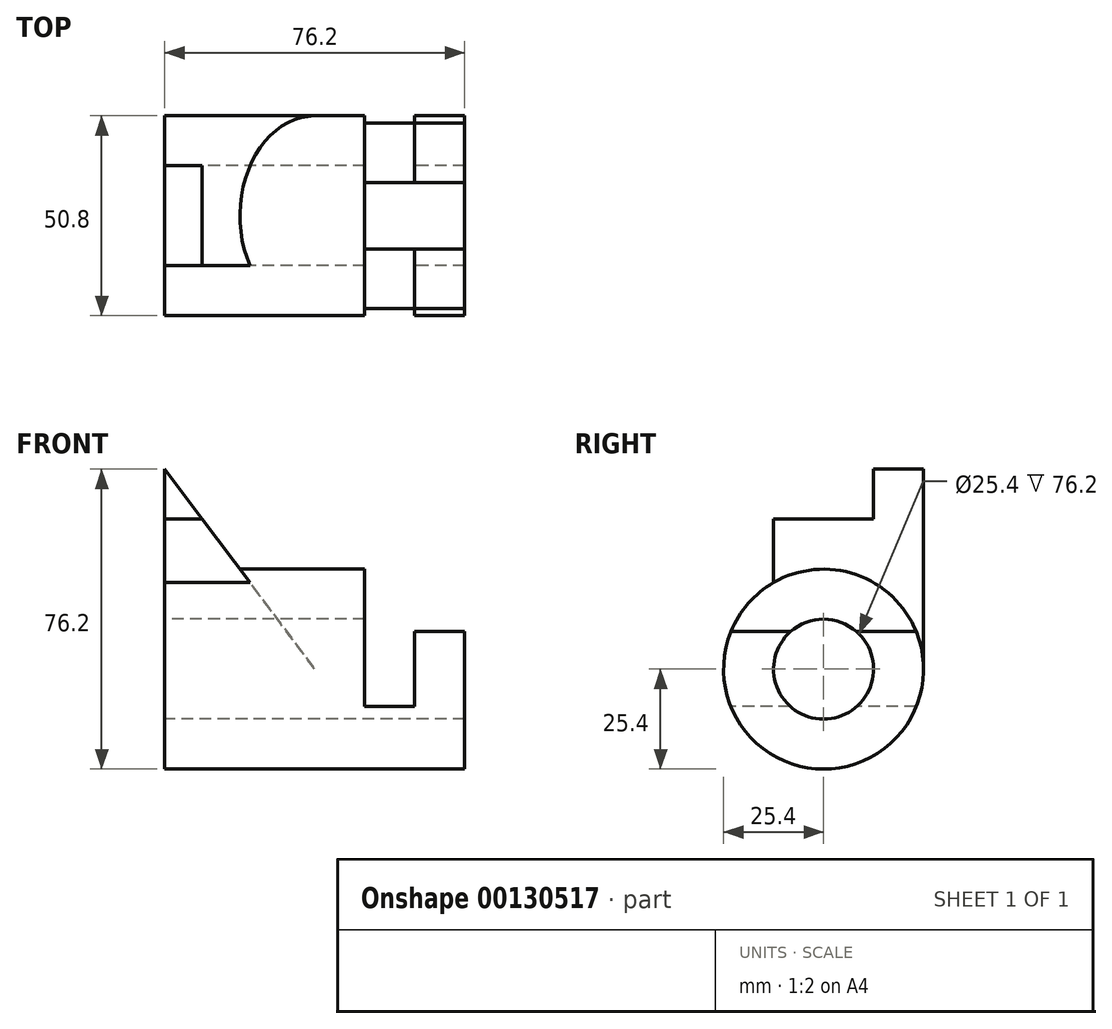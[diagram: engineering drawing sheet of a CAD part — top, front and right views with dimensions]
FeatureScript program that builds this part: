
annotation { "Feature Type Name" : "Feature", "Feature Type Description" : "" }
export const myFeature = defineFeature(function(context is Context, id is Id, definition is map)
    precondition{}
    {
        {
            var Q0;
            Q0=qCreatedBy(makeId("Right.planeOp"),FACE);
            var sketch = newSketch(context, id + "F0", { "sketchPlane" : qUnion([Q0])});
            skCircle(sketch, "E0", {"center": v(0, 0) * mm, "radius": 25.4 * mm});
            skCircle(sketch, "E1", {"center": v(0, 0) * mm, "radius": 12.7 * mm});
            skSolve(sketch);
        }
        {
            var Q0;
            Q0=makeQuery(id+"F0.imprint","IMPRINT",FACE,{"disambiguationData":[TD([[makeQuery(id+"F0.imprint","IMPRINT",EDGE,{"derivedFrom":sQuery(id+"F0.wireOp",EDGE,"E0")}),1.0]])]});
            extrude(context, id + "F1", {"entities" : qUnion([Q0]), "endBound" : BoundingType.SYMMETRIC, "depth" : 76.2 * mm});
        }
        {
            var Q0;
            Q0=qCreatedBy(makeId("Front.planeOp"),FACE);
            var sketch = newSketch(context, id + "F2", { "sketchPlane" : qUnion([Q0])});
            skLineSegment(sketch, "E2.bottom", {"start": v(0, 0) * mm, "end": v(-38.1, 0) * mm});
            skLineSegment(sketch, "E2.top", {"start": v(0, 50.8) * mm, "end": v(-38.1, 50.8) * mm});
            skLineSegment(sketch, "E2.left", {"start": v(0, 0) * mm, "end": v(0, 50.8) * mm});
            skLineSegment(sketch, "E2.right", {"start": v(-38.1, 0) * mm, "end": v(-38.1, 50.8) * mm});
            skLineSegment(sketch, "E3", {"start": v(-38.1, 50.8) * mm, "end": v(0, 0) * mm});
            skSolve(sketch);
        }
        {
            var Q0;
            Q0=makeQuery(id+"F2.imprint","IMPRINT",FACE,{"disambiguationData":[TD([[makeQuery(id+"F2.imprint","IMPRINT",EDGE,{"derivedFrom":sQuery(id+"F2.wireOp",EDGE,"E2.bottom")}),-1.0]])]});
            extrude(context, id + "F3", {"entities" : qUnion([Q0]), "operationType" : NewBodyOperationType.ADD, "depth" : 12.7 * mm, "hasSecondDirection" : true, "secondDirectionOppositeDirection" : true, "secondDirectionDepth" : 25.4 * mm});
        }
        {
            var Q0;
            Q0=makeQuery(id+"F0.imprint","IMPRINT",FACE,{"disambiguationData":[TD([[makeQuery(id+"F0.imprint","IMPRINT",EDGE,{"derivedFrom":sQuery(id+"F0.wireOp",EDGE,"E1")}),1.0]])]});
            extrude(context, id + "F4", {"entities" : qUnion([Q0]), "operationType" : NewBodyOperationType.REMOVE, "endBound" : BoundingType.THROUGH_ALL, "oppositeDirection" : true, "depth" : 25.4 * mm});
        }
        {
            var Q0;
            Q0=makeQuery(id+"F3.boolean.opBoolean","MERGE",FACE,{"derivedFrom":[makeQuery(id+"F1.opExtrude","CAP_FACE",FACE,{"disambiguationData":[OSD([sQuery(id+"F0.wireOp",EDGE,"E0"),sQuery(id+"F0.wireOp",EDGE,"E1")])],"isStart":true}),makeQuery(id+"F3.opExtrude","SWEPT_FACE",FACE,{"disambiguationData":[OSD([sQuery(id+"F2.wireOp",EDGE,"E2.right")])]})]});
            var sketch = newSketch(context, id + "F5", { "sketchPlane" : qUnion([Q0])});
            skLineSegment(sketch, "E4.bottom", {"start": v(12.7, 50.8) * mm, "end": v(-12.7, 50.8) * mm});
            skLineSegment(sketch, "E4.top", {"start": v(12.7, 38.1) * mm, "end": v(-12.7, 38.1) * mm});
            skLineSegment(sketch, "E4.left", {"start": v(12.7, 50.8) * mm, "end": v(12.7, 38.1) * mm});
            skLineSegment(sketch, "E4.right", {"start": v(-12.7, 50.8) * mm, "end": v(-12.7, 38.1) * mm});
            skSolve(sketch);
        }
        {
            var Q0;
            Q0=makeQuery(id+"F5.imprint","IMPRINT",FACE,{"disambiguationData":[TD([[makeQuery(id+"F5.imprint","IMPRINT",EDGE,{"derivedFrom":sQuery(id+"F5.wireOp",EDGE,"E4.bottom")}),1.0]])]});
            extrude(context, id + "F6", {"entities" : qUnion([Q0]), "operationType" : NewBodyOperationType.REMOVE, "endBound" : BoundingType.THROUGH_ALL, "oppositeDirection" : true, "depth" : 25.4 * mm});
        }
        {
            var Q0;
            Q0=qCreatedBy(makeId("Front.planeOp"),FACE);
            cPlane(context, id + "F7", {"entities" : qUnion([Q0]), "cplaneType" : CPlaneType.OFFSET, "offset" : 25.4 * mm, "width" : 152.4 * mm, "height" : 152.4 * mm});
        }
        {
            var Q0;
            Q0=qCreatedBy(id+"F7.planeOp",FACE);
            var sketch = newSketch(context, id + "F8", { "sketchPlane" : qUnion([Q0])});
            skLineSegment(sketch, "E5", {"start": v(-43.3, 0) * mm, "end": v(64.1, 0) * mm, "construction": true});
            skLineSegment(sketch, "E6.bottom", {"start": v(12.7, -9.53) * mm, "end": v(25.4, -9.53) * mm});
            skLineSegment(sketch, "E6.left", {"start": v(12.7, -9.53) * mm, "end": v(12.7, 25.4) * mm});
            skLineSegment(sketch, "E6.right", {"start": v(25.4, -9.53) * mm, "end": v(25.4, 9.53) * mm});
            skLineSegment(sketch, "E7.bottom", {"start": v(25.4, 9.53) * mm, "end": v(38.1, 9.53) * mm});
            skLineSegment(sketch, "E7.right", {"start": v(38.1, 9.53) * mm, "end": v(38.1, 25.4) * mm});
            skLineSegment(sketch, "E8", {"start": v(12.7, 25.4) * mm, "end": v(38.1, 25.4) * mm});
            skLineSegment(sketch, "E9", {"start": v(75.61, 25.4) * mm, "end": v(-100.94, 25.4) * mm, "construction": true});
            skLineSegment(sketch, "E10", {"start": v(38.1, 45.34) * mm, "end": v(38.1, -46.71) * mm, "construction": true});
            skSolve(sketch);
        }
        {
            var Q0;
            Q0=makeQuery(id+"F8.imprint","IMPRINT",FACE,{"disambiguationData":[TD([[makeQuery(id+"F8.imprint","IMPRINT",EDGE,{"derivedFrom":sQuery(id+"F8.wireOp",EDGE,"E6.bottom")}),1.0]])]});
            extrude(context, id + "F9", {"entities" : qUnion([Q0]), "operationType" : NewBodyOperationType.REMOVE, "endBound" : BoundingType.THROUGH_ALL, "oppositeDirection" : true, "depth" : 25.4 * mm});
        }
    });
